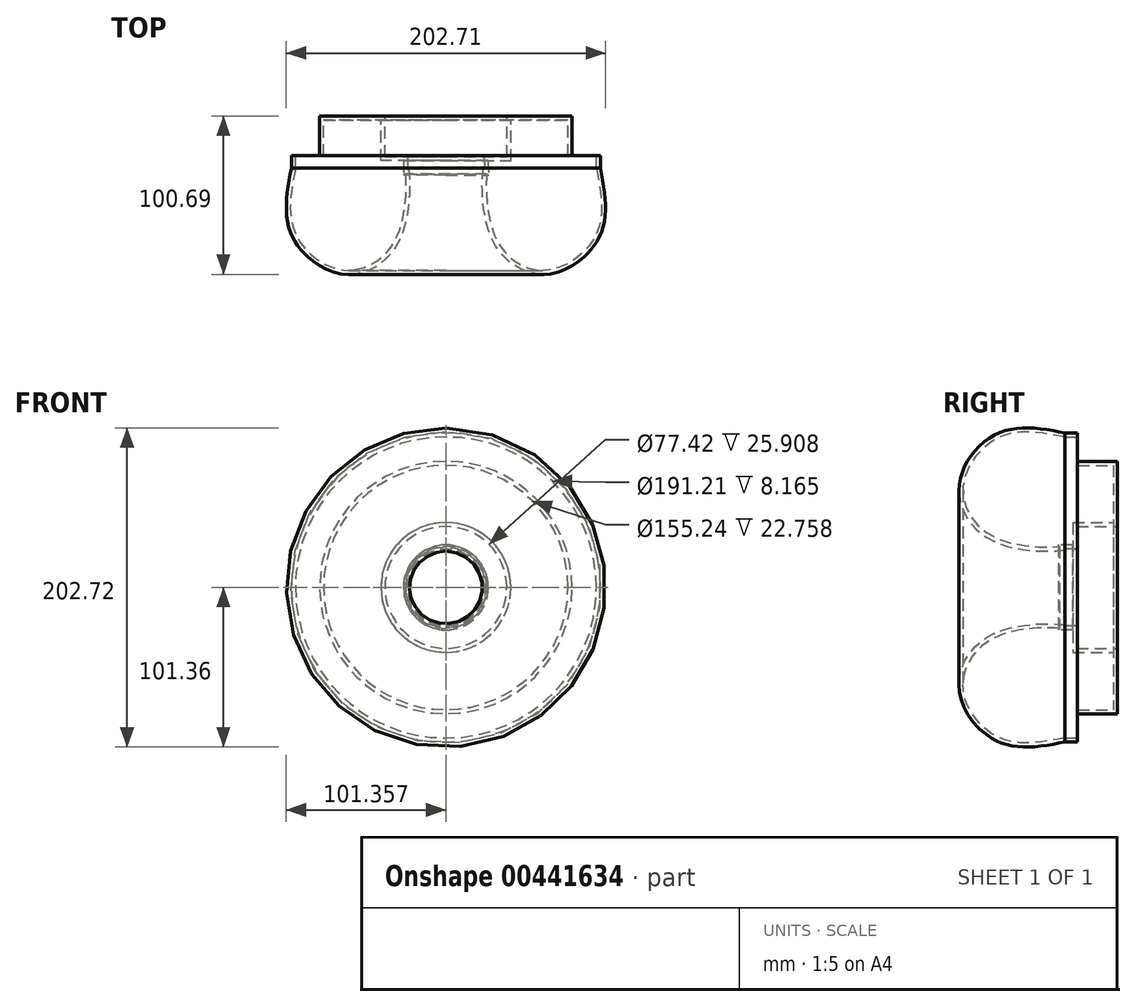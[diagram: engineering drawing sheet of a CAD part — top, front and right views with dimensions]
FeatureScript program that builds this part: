
annotation { "Feature Type Name" : "Feature", "Feature Type Description" : "" }
export const myFeature = defineFeature(function(context is Context, id is Id, definition is map)
    precondition{}
    {
        {
            var Q0;
            Q0=qCreatedBy(makeId("Top.planeOp"),FACE);
            var sketch = newSketch(context, id + "F0", { "sketchPlane" : qUnion([Q0])});
            skLineSegment(sketch, "E0", {"start": v(-25.6, 55.63) * mm, "end": v(15.85, 55.63) * mm});
            skLineSegment(sketch, "E1", {"start": v(15.85, 55.63) * mm, "end": v(15.85, 30.33) * mm});
            skLineSegment(sketch, "E2", {"start": v(15.85, 30.33) * mm, "end": v(33.83, 30.33) * mm});
            skLineSegment(sketch, "E3", {"start": v(33.83, 30.33) * mm, "end": v(33.83, 22.4) * mm});
            skFitSpline(sketch, "E4", {"points": [v(33.83, 22.4) * mm, v(33.83, -19.66) * mm, v(0, -44.96) * mm, v(-36.27, -19.96) * mm, v(-40.23, 22.4) * mm, v(-39.93, 22.4) * mm], "startDerivative": vector(34.35, -180.2) * mm, "endDerivative": vector(14.67, -7.98) * mm});
            skLineSegment(sketch, "E5", {"start": v(-25.6, 55.63) * mm, "end": v(-25.6, 29.72) * mm});
            skLineSegment(sketch, "E6", {"start": v(-25.6, 29.72) * mm, "end": v(-40.03, 29.72) * mm});
            skLineSegment(sketch, "E7", {"start": v(-40.03, 29.72) * mm, "end": v(-39.93, 22.4) * mm});
            skLineSegment(sketch, "E8", {"start": v(-64.31, 61.42) * mm, "end": v(-64.31, -48.62) * mm});
            skSolve(sketch);
        }
        {
            var Q0;
            Q0=makeQuery(id+"F0.imprint","IMPRINT",FACE,{"disambiguationData":[TD([[makeQuery(id+"F0.imprint","IMPRINT",EDGE,{"derivedFrom":sQuery(id+"F0.wireOp",EDGE,"E0")}),-1.0]])]});
            var Q1;
            Q1=sQuery(id+"F0.wireOp",EDGE,"E8");
            revolve(context, id + "F1", {"entities" : qUnion([Q0]), "axis" : qUnion([Q1]), "revolveType" : RevolveType.FULL});
        }
        {
            var Q0;
            Q0=makeQuery(id+"F1.opRevolve","SWEPT_FACE",FACE,{"disambiguationData":[OSD([sQuery(id+"F0.wireOp",EDGE,"E2")])]});
            shell(context, id + "F2", {"entities" : qUnion([Q0]), "thickness" : 2.54 * mm});
        }
    });
